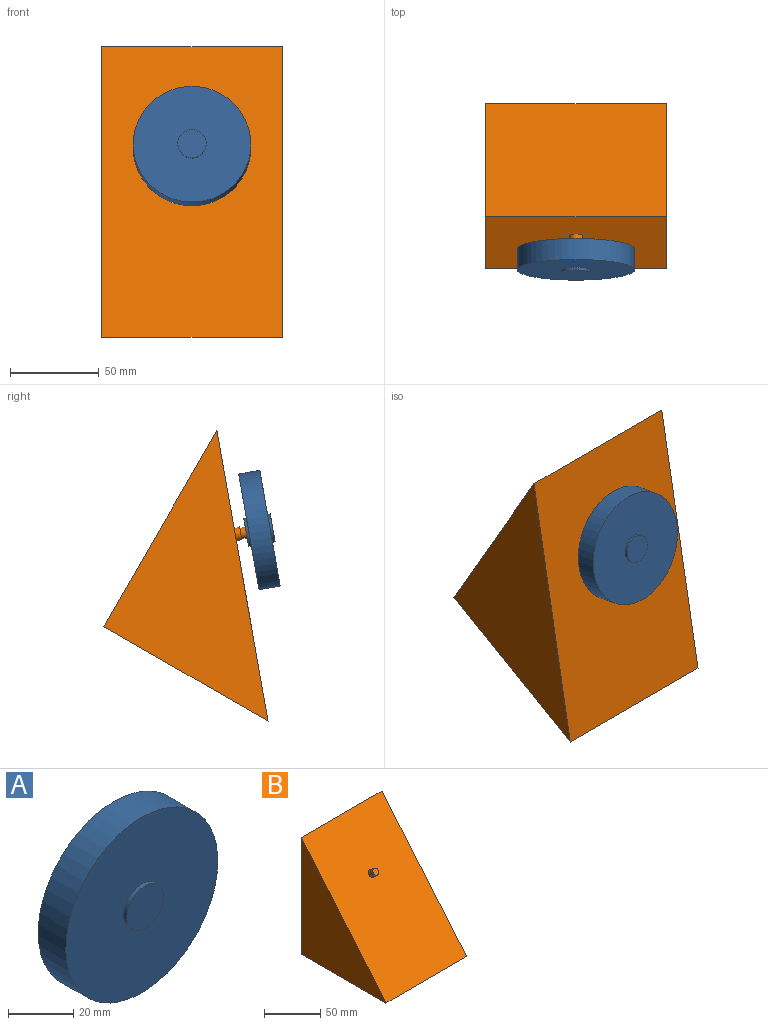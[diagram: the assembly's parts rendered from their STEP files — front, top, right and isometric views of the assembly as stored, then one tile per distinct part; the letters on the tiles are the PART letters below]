
ASSEMBLY  parts=2 mates=1
PART A: 7 faces, bbox 66x15x66 mm
  f0: cylinder r=8mm len=16mm, axis (0,1,0), area 75.4mm2, adj f1,f4
  f1: plane 16x16mm, normal (0,-1,0), area 201.1mm2, adj f0
  f2: cylinder r=33mm len=66mm, axis (0,-1,0), area 2488.1mm2, adj f3,f4
  f3: plane 66x66mm, normal (0,1,0), area 3220.1mm2, adj f2,f5
  f4: plane 66x66mm, normal (0,-1,0), area 3220.1mm2, adj f0,f2
  f5: cylinder r=8mm len=16mm, axis (0,-1,0), area 75.4mm2, adj f3,f6
  f6: plane 16x16mm, normal (0,1,0), area 201.1mm2, adj f5
PART B: 9 faces, bbox 101.6x106.6x127 mm
  f0: plane 127x106.57mm, normal (0,-0.77,0.64), area 16802mm2, adj f1,f2,f3,f4,f5
  f1: plane 106.57x101.6mm, normal (0,0,-1), area 10827.1mm2, adj f0,f2,f3,f4
  f2: plane 127x101.6mm, normal (0,1,0), area 12903.2mm2, adj f0,f1,f3,f4
  f3: plane 127x106.57mm, normal (1,0,0), area 6766.9mm2, adj f0,f1,f2
  f4: plane 127x106.57mm, normal (-1,0,0), area 6766.9mm2, adj f0,f1,f2
  f5: cylinder r=3.65mm len=7.64mm, axis (0,0.77,-0.64), area 72.8mm2, adj f0,f6
  f6: plane 7.3x5.59mm, normal (0,-0.77,0.64), area 11.1mm2, adj f5,f7
  f7: cylinder r=3.13mm len=6.84mm, axis (0,0.77,-0.64), area 62.5mm2, adj f6,f8
  f8: plane 6.26x4.8mm, normal (0,-0.77,0.64), area 30.8mm2, adj f7
PLACE A rot(axis=(-1,0,0),10deg) t=(-6.47,-13.22,1.97)mm
PLACE B rot(axis=(1,0,0),30deg) t=(-57.27,-12.19,-106.5)mm
MATE fastened A.f0 <-> B.f5  axis (0,0.98,-0.17) through (-6.47,0.07,-0.38)mm
